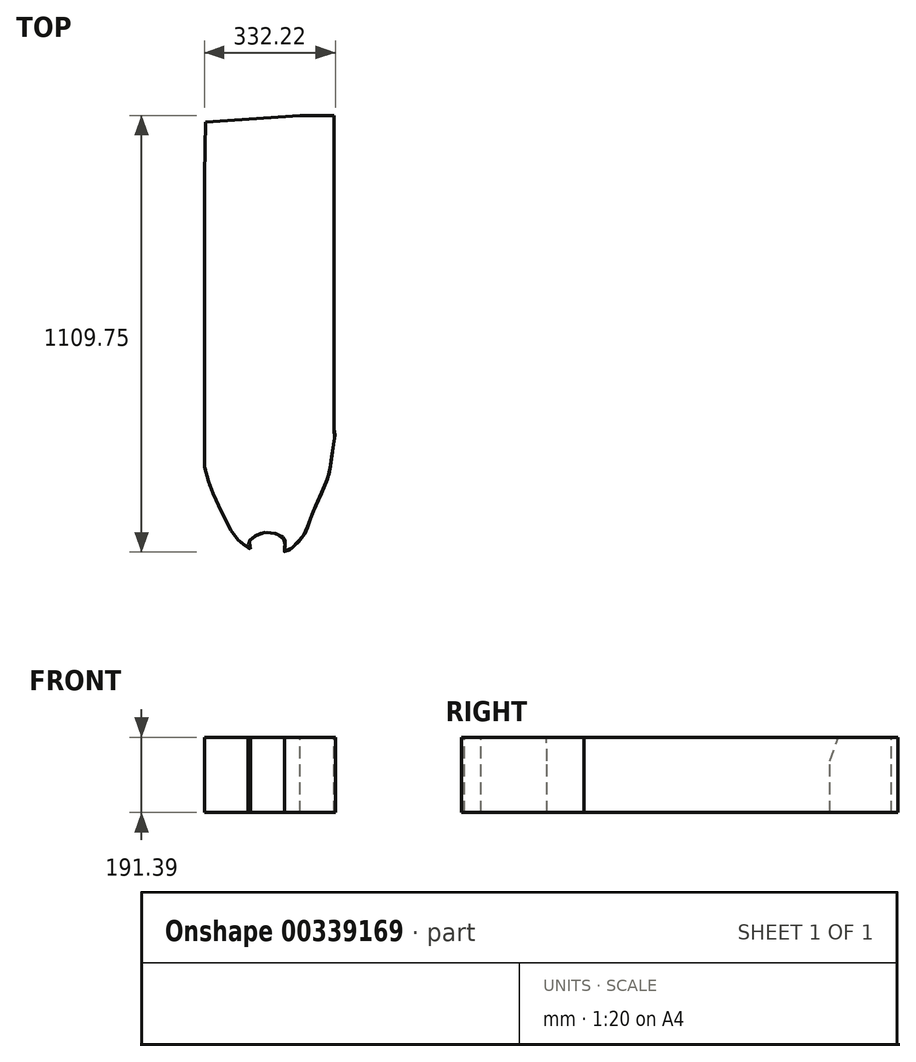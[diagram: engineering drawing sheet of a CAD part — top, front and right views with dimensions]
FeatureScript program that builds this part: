
annotation { "Feature Type Name" : "Feature", "Feature Type Description" : "" }
export const myFeature = defineFeature(function(context is Context, id is Id, definition is map)
    precondition{}
    {
        {
            var Q0;
            Q0=qCreatedBy(makeId("Front.planeOp"),FACE);
            cPlane(context, id + "F0", {"entities" : qUnion([Q0]), "cplaneType" : CPlaneType.OFFSET, "offset" : (1115.5 / 2) * mm, "width" : 150 * mm, "height" : 150 * mm});
        }
        {
            var Q0;
            Q0=qCreatedBy(makeId("Right.planeOp"),FACE);
            cPlane(context, id + "F1", {"entities" : qUnion([Q0]), "cplaneType" : CPlaneType.OFFSET, "offset" : (499.5 / 2) * mm, "width" : 150 * mm, "height" : 150 * mm});
        }
        {
            var Q0;
            Q0=qCreatedBy(makeId("Front.planeOp"),FACE);
            cPlane(context, id + "F2", {"entities" : qUnion([Q0]), "cplaneType" : CPlaneType.OFFSET, "offset" : 557.75 * mm, "oppositeDirection" : true, "width" : 150 * mm, "height" : 150 * mm});
        }
        {
            var Q0;
            Q0=qCreatedBy(id+"F1.planeOp",FACE);
            var sketch = newSketch(context, id + "F3", { "sketchPlane" : qUnion([Q0])});
            skLineSegment(sketch, "E0", {"start": v(0, 0) * mm, "end": v(-750.5, 0) * mm, "construction": true});
            skLineSegment(sketch, "E1", {"start": v(0, 0) * mm, "end": v(0, 318.41) * mm, "construction": true});
            skLineSegment(sketch, "E2", {"start": v(-230.75, -125.19) * mm, "end": v(280.5, -125.19) * mm});
            skLineSegment(sketch, "E3", {"start": v(471.3, -116.98) * mm, "end": v(504.8, -116.98) * mm});
            skPoint(sketch, "E4.startSnap0", {"position": v(367.44, 23.35) * mm});
            skCircle(sketch, "E5", {"center": v(-324.04, -73.29) * mm, "radius": 84.5 * mm});
            skCircle(sketch, "E6", {"center": v(377.29, -64.61) * mm, "radius": 89.5 * mm});
            skLineSegment(sketch, "E7", {"start": v(-324.04, -73.29) * mm, "end": v(-324.04, -346.73) * mm, "construction": true});
            skLineSegment(sketch, "E8", {"start": v(377.29, -64.61) * mm, "end": v(377.29, -343.02) * mm, "construction": true});
            skLineSegment(sketch, "E9", {"start": v(-557.75, -130.16) * mm, "end": v(-414.75, -130.16) * mm});
            skLineSegment(sketch, "E10", {"start": v(-414.75, -130.16) * mm, "end": v(-414.75, 120.13) * mm, "construction": true});
            skLineSegment(sketch, "E11", {"start": v(-230.75, -125.19) * mm, "end": v(-230.75, 131.26) * mm, "construction": true});
            skLineSegment(sketch, "E12", {"start": v(280.5, -125.19) * mm, "end": v(280.5, 291.59) * mm, "construction": true});
            skLineSegment(sketch, "E13", {"start": v(471.3, -116.98) * mm, "end": v(471.3, -275.96) * mm, "construction": true});
            skFitSpline(sketch, "E14", {"points": [v(504.8, -116.98) * mm, v(528.88, -99.54) * mm, v(543.3, -12.03) * mm], "startDerivative": vector(74.99, 30.55) * mm, "endDerivative": vector(8.08, 167.36) * mm, "construction": true});
            skLineSegment(sketch, "E15", {"start": v(543.3, -12.03) * mm, "end": v(543.3, -246.55) * mm, "construction": true});
            skLineSegment(sketch, "E16", {"start": v(-324.04, -73.29) * mm, "end": v(-275.98, -73.29) * mm});
            skSolve(sketch);
        }
        {
            var Q0;
            Q0=qCreatedBy(makeId("Top.planeOp"),FACE);
            cPlane(context, id + "F4", {"entities" : qUnion([Q0]), "cplaneType" : CPlaneType.OFFSET, "offset" : 150.5 * mm, "width" : 150 * mm, "height" : 150 * mm});
        }
        {
            var Q0;
            Q0=qCreatedBy(id+"F4.planeOp",FACE);
            var sketch = newSketch(context, id + "F5", { "sketchPlane" : qUnion([Q0])});
            skLineSegment(sketch, "E17", {"start": v(-192.82, -177.73) * mm, "end": v(-274.39, -177.73) * mm, "construction": true});
            skLineSegment(sketch, "E18", {"start": v(-75.63, -543.84) * mm, "end": v(-326.52, -543.84) * mm, "construction": true});
            skLineSegment(sketch, "E19", {"start": v(-179.26, -240.88) * mm, "end": v(-344.31, -240.88) * mm, "construction": true});
            skLineSegment(sketch, "E20", {"start": v(-102.17, -512.68) * mm, "end": v(-401.64, -512.68) * mm, "construction": true});
            skFitSpline(sketch, "E21", {"points": [v(-179.26, -240.88) * mm, v(-122.5, -269.94) * mm, v(-18.23, -301) * mm, v(76.07, -285.47) * mm, v(159.27, -240.88) * mm, v(159.27, -271.05) * mm, v(149.29, -338.72) * mm, v(135.98, -382) * mm, v(93.82, -480.72) * mm, v(81.62, -510.68) * mm, v(34.29, -551.75) * mm, v(34.4, -520.5) * mm, v(0, -502.87) * mm, v(-30.25, -505.23) * mm, v(-49.05, -516.98) * mm, v(-58.46, -531.08) * mm, v(-52.88, -543.58) * mm, v(-75.63, -528.19) * mm, v(-96.26, -506.27) * mm, v(-150.08, -397.54) * mm, v(-165.79, -349.37) * mm, v(-179.26, -240.88) * mm]});
            skLineSegment(sketch, "E22.top", {"start": v(0, 1282.63) * mm, "end": v(-334.43, 1282.63) * mm});
            skPoint(sketch, "E22.middle", {"position": v(-167.21, 541.2) * mm});
            skLineSegment(sketch, "E23", {"start": v(-167.21, 541.2) * mm, "end": v(-179.26, -240.88) * mm});
            skLineSegment(sketch, "E24", {"start": v(159.27, -240.88) * mm, "end": v(159.27, 563.75) * mm});
            skLineSegment(sketch, "E25", {"start": v(-167.21, 541.2) * mm, "end": v(159.27, 563.75) * mm});
            skSolve(sketch);
        }
        {
            var Q0;
            Q0=qCreatedBy(id+"F2.planeOp",FACE);
            var sketch = newSketch(context, id + "F6", { "sketchPlane" : qUnion([Q0])});
            skLineSegment(sketch, "E26", {"start": v(0, 0) * mm, "end": v(0, 309.67) * mm, "construction": true});
            skLineSegment(sketch, "E27", {"start": v(0, 0) * mm, "end": v(437.55, 0) * mm, "construction": true});
            skLineSegment(sketch, "E28", {"start": v(169.63, 48.25) * mm, "end": v(169.63, -128.25) * mm});
            skLineSegment(sketch, "E29.MirrorCS", {"start": v(-169.63, 48.25) * mm, "end": v(-169.63, -128.25) * mm});
            skLineSegment(sketch, "E30", {"start": v(169.63, 108.7) * mm, "end": v(-169.3, 108.7) * mm});
            skLineSegment(sketch, "E31", {"start": v(169.63, 108.7) * mm, "end": v(169.63, 48.25) * mm});
            skLineSegment(sketch, "E32", {"start": v(-169.3, 108.7) * mm, "end": v(-169.63, 48.25) * mm});
            skLineSegment(sketch, "E33", {"start": v(169.63, -128.25) * mm, "end": v(-169.63, -128.25) * mm});
            skSolve(sketch);
        }
        {
            var Q0;
            Q0 = qSketchRegion(id + "F6", true);
            extrude(context, id + "F7", {"entities" : qUnion([Q0]), "depth" : 1123 * mm});
        }
        {
            var Q0;
            Q0 = qSketchRegion(id + "F3", true);
            var Q1;
            Q1=sQuery(id+"F3.wireOp",EDGE,"E9");
            var Q2;
            Q2=sQuery(id+"F3.wireOp",EDGE,"E5");
            var Q3;
            Q3=sQuery(id+"F3.wireOp",EDGE,"E2");
            var Q4;
            Q4=sQuery(id+"F3.wireOp",EDGE,"E6");
            var Q5;
            Q5=sQuery(id+"F3.wireOp",EDGE,"E3");
            extrude(context, id + "F8", {"entities" : qUnion([Q0]), "bodyType" : ToolBodyType.SURFACE, "operationType" : NewBodyOperationType.ADD, "surfaceEntities" : qUnion([Q1, Q2, Q3, Q4, Q5]), "oppositeDirection" : true, "depth" : 519 * mm});
        }
        {
            var Q0;
            Q0 = qSketchRegion(id + "F5", true);
            var Q1;
            Q1=sQuery(id+"F5.wireOp",EDGE,"E24");
            var Q2;
            Q2=sQuery(id+"F5.wireOp",EDGE,"E23");
            var Q3;
            Q3=sQuery(id+"F5.wireOp",EDGE,"E25");
            extrude(context, id + "F9", {"entities" : qUnion([Q0]), "bodyType" : ToolBodyType.SURFACE, "operationType" : NewBodyOperationType.REMOVE, "surfaceEntities" : qUnion([Q1, Q2, Q3]), "oppositeDirection" : true, "depth" : 290 * mm});
        }
        {
            var Q0;
            Q0 = qSketchRegion(id + "F5", true);
            var Q1;
            Q1=sQuery(id+"F5.wireOp",EDGE,"E21");
            extrude(context, id + "F10", {"entities" : qUnion([Q0]), "operationType" : NewBodyOperationType.INTERSECT, "surfaceEntities" : qUnion([Q1]), "oppositeDirection" : true, "depth" : 233.2 * mm});
        }
    });
